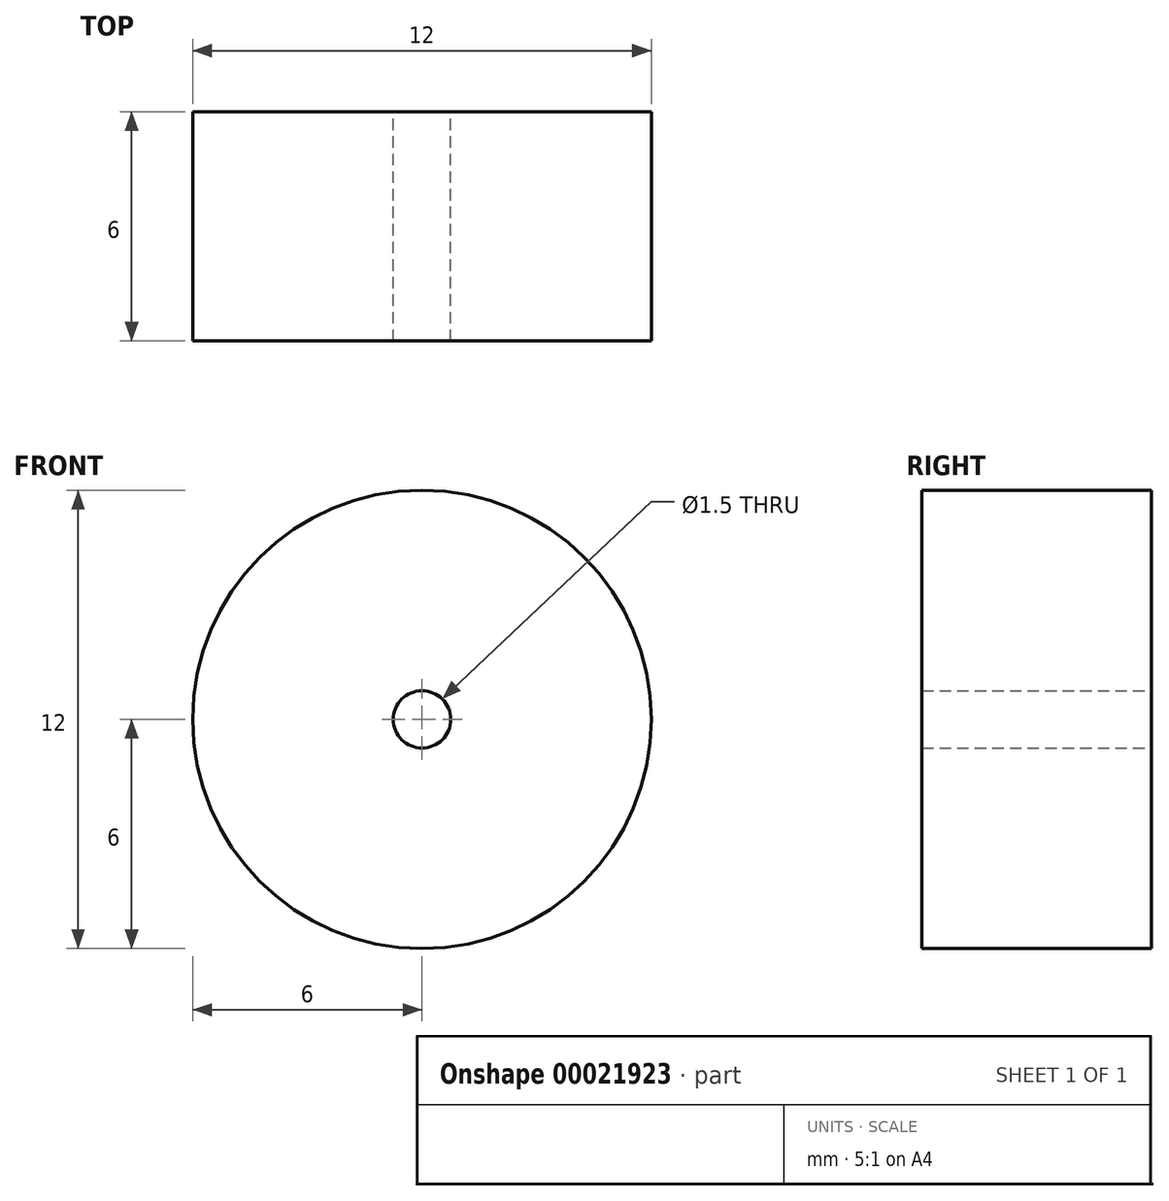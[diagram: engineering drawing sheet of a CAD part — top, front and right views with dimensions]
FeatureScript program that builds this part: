
annotation { "Feature Type Name" : "Feature", "Feature Type Description" : "" }
export const myFeature = defineFeature(function(context is Context, id is Id, definition is map)
    precondition{}
    {
        {
            var Q0;
            Q0=qCreatedBy(makeId("Front.planeOp"),FACE);
            var sketch = newSketch(context, id + "F0", { "sketchPlane" : qUnion([Q0])});
            skCircle(sketch, "E0", {"center": v(0, 0) * mm, "radius": 6 * mm});
            skCircle(sketch, "E1", {"center": v(0, 0) * mm, "radius": 0.75 * mm});
            skSolve(sketch);
        }
        {
            var Q0;
            Q0=makeQuery(id+"F0.imprint","IMPRINT",FACE,{"disambiguationData":[TD([[makeQuery(id+"F0.imprint","IMPRINT",EDGE,{"derivedFrom":sQuery(id+"F0.wireOp",EDGE,"E0")}),1.0]])]});
            extrude(context, id + "F1", {"entities" : qUnion([Q0]), "endBound" : BoundingType.SYMMETRIC, "depth" : 6 * mm});
        }
    });
